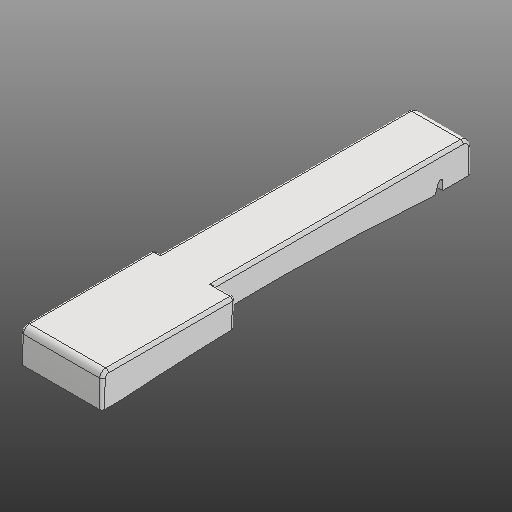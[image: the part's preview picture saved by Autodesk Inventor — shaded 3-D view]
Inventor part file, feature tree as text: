
AUTODESK INVENTOR PART (.ipt)
format: ipt  version: 2020 (Build 240168000, 168)  size: 329,728 bytes
history: native  units: in
note: dims shown in document units (in); Inventor stores cm internally (conversion verified against a paired STEP export)
features: extrude x4, other x3, fillet x2
ambient origin geometry x8: Origin, YZ Plane, XZ Plane, XY Plane, X Axis, Y Axis, Z Axis, Center Point
bodies: Solid1 (feature_tree)
feature tree (9):
  other  "Slot Start Plane"
  other  "Key Profile"
  extrude  "Upper (u)"  TaperAngle=0.0deg  [1 undecoded]
  extrude  "Lower (d)"  TaperAngle=0.0deg  [1 undecoded]
  extrude  "Protrusion Cutout"  Depth=0.0591in
  fillet  "Front Fillet"  Radius=0.1374in
  extrude  "Slot"  [1 undecoded]
  fillet  "Edge Softening"  Radius=0.0787in
  other  "Slot Sketch"
note: 3 required parameter values undecoded (feature->parameter linkage not recoverable at this tier; creation-order binding heuristic only, values carry confidence <= 0.55)
